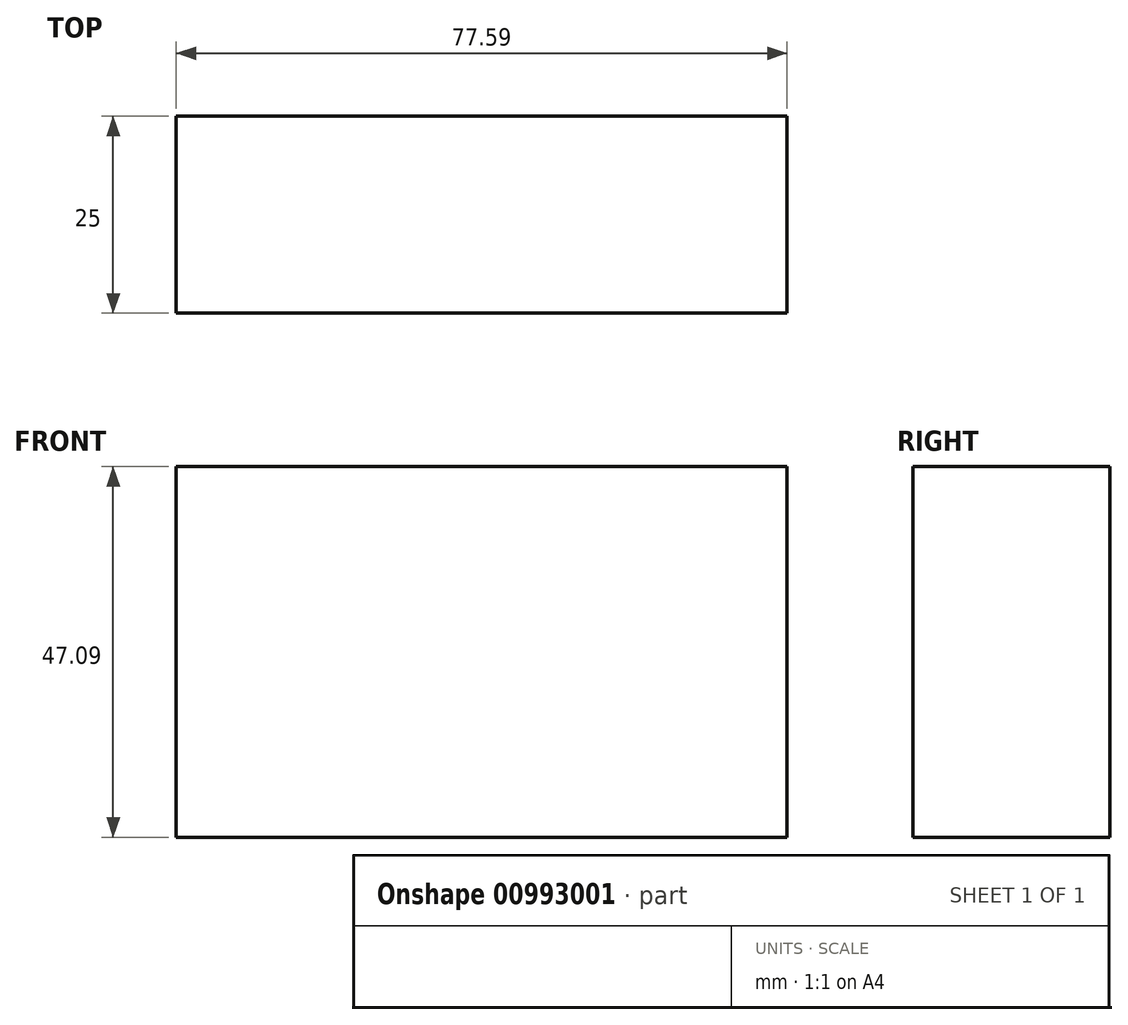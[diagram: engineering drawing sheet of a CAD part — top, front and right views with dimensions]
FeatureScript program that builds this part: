
annotation { "Feature Type Name" : "Feature", "Feature Type Description" : "" }
export const myFeature = defineFeature(function(context is Context, id is Id, definition is map)
    precondition{}
    {
        {
            var Q0;
            Q0=qCreatedBy(makeId("Front.planeOp"),FACE);
            var sketch = newSketch(context, id + "F0", { "sketchPlane" : qUnion([Q0])});
            skLineSegment(sketch, "E0.bottom", {"start": v(0, 0) * mm, "end": v(77.59, 0) * mm});
            skLineSegment(sketch, "E0.top", {"start": v(0, 47.1) * mm, "end": v(77.59, 47.1) * mm});
            skLineSegment(sketch, "E0.left", {"start": v(0, 0) * mm, "end": v(0, 47.1) * mm});
            skLineSegment(sketch, "E0.right", {"start": v(77.59, 0) * mm, "end": v(77.59, 47.1) * mm});
            skSolve(sketch);
        }
        {
            var Q0;
            Q0 = qSketchRegion(id + "F0", true);
            extrude(context, id + "F1", {"entities" : qUnion([Q0]), "depth" : 25 * mm, "offsetDistance" : 25 * mm});
        }
    });
